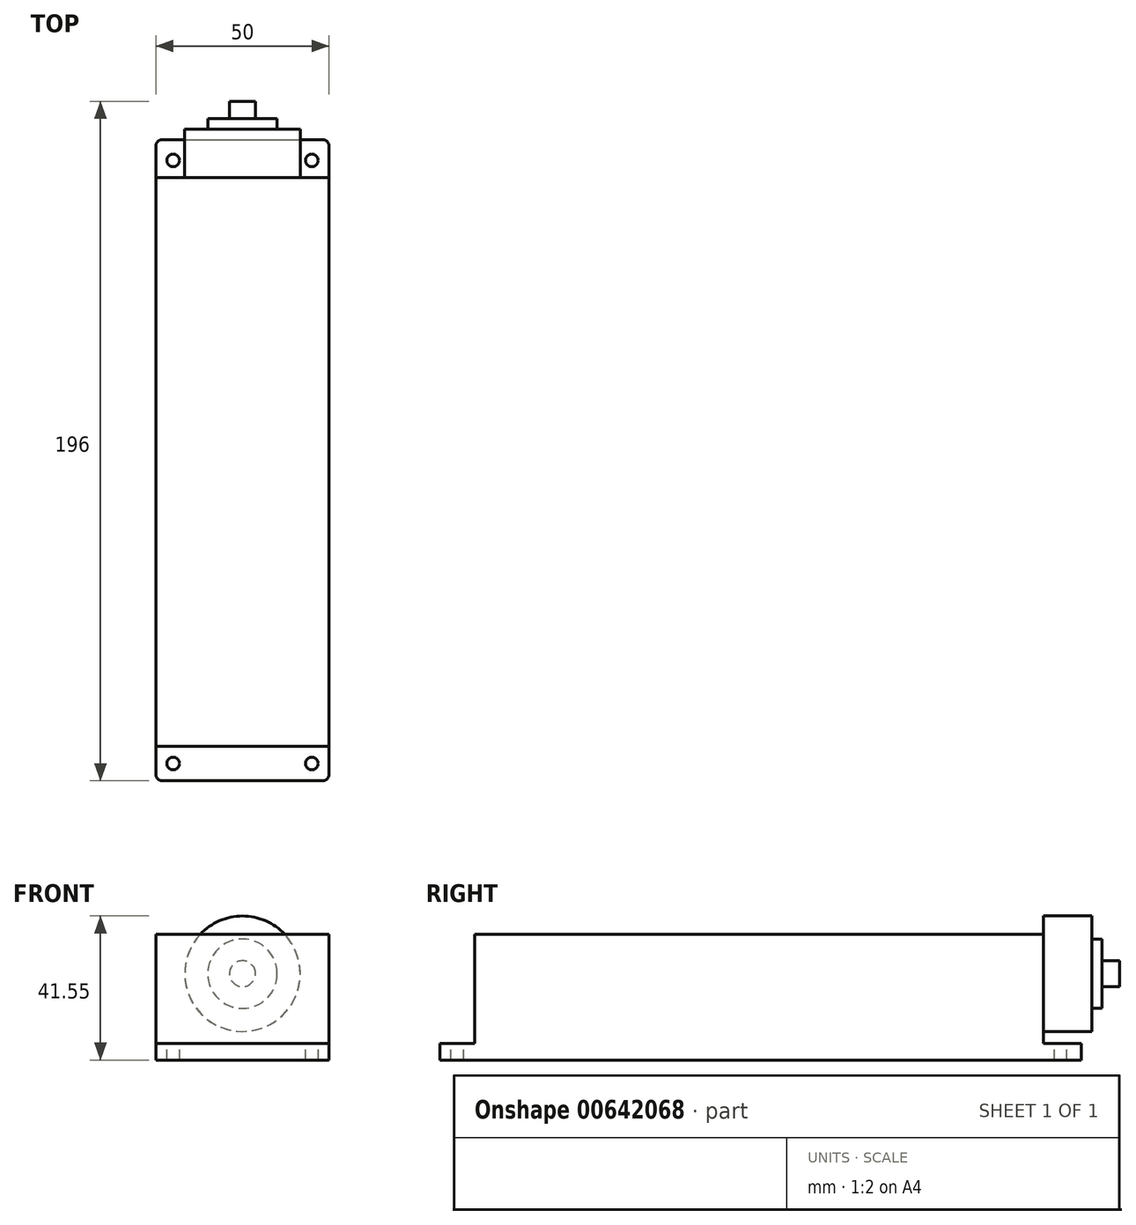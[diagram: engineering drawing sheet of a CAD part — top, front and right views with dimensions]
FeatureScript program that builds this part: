
annotation { "Feature Type Name" : "Feature", "Feature Type Description" : "" }
export const myFeature = defineFeature(function(context is Context, id is Id, definition is map)
    precondition{}
    {
        {
            var Q0;
            Q0=qCreatedBy(makeId("Top.planeOp"),FACE);
            var sketch = newSketch(context, id + "F0", { "sketchPlane" : qUnion([Q0])});
            skLineSegment(sketch, "E0.bottom", {"start": v(2, 0) * mm, "end": v(48, 0) * mm});
            skLineSegment(sketch, "E0.top", {"start": v(2, 185) * mm, "end": v(48, 185) * mm});
            skLineSegment(sketch, "E0.left", {"start": v(0, 2) * mm, "end": v(0, 183) * mm});
            skLineSegment(sketch, "E0.right", {"start": v(50, 2) * mm, "end": v(50, 183) * mm});
            skPoint(sketch, "E1.visualSharp", {"position": v(0, 185) * mm});
            skArc(sketch, "E1.filletArc", {"start": v(2, 185) * mm, "mid": v(0.59, 184.41) * mm, "end": v(0, 183) * mm});
            skPoint(sketch, "E2.visualSharp", {"position": v(50, 185) * mm});
            skArc(sketch, "E2.filletArc", {"start": v(50, 183) * mm, "mid": v(49.41, 184.41) * mm, "end": v(48, 185) * mm});
            skPoint(sketch, "E3.visualSharp", {"position": v(0, 0) * mm});
            skArc(sketch, "E3.filletArc", {"start": v(0, 2) * mm, "mid": v(0.59, 0.59) * mm, "end": v(2, 0) * mm});
            skPoint(sketch, "E4.visualSharp", {"position": v(50, 0) * mm});
            skArc(sketch, "E4.filletArc", {"start": v(48, 0) * mm, "mid": v(49.41, 0.59) * mm, "end": v(50, 2) * mm});
            skSolve(sketch);
        }
        {
            var Q0;
            Q0 = qSketchRegion(id + "F0", true);
            extrude(context, id + "F1", {"entities" : qUnion([Q0]), "depth" : 4.75 * mm, "offsetDistance" : 25 * mm});
        }
        {
            var Q0;
            Q0=makeQuery(id+"F1.opExtrude","CAP_FACE",FACE,{"disambiguationData":[OSD([sQuery(id+"F0.wireOp",EDGE,"E0.bottom"),sQuery(id+"F0.wireOp",EDGE,"E0.top"),sQuery(id+"F0.wireOp",EDGE,"E0.left"),sQuery(id+"F0.wireOp",EDGE,"E0.right")])],"isStart":false});
            var sketch = newSketch(context, id + "F2", { "sketchPlane" : qUnion([Q0])});
            skLineSegment(sketch, "E5.bottom", {"start": v(0, 174) * mm, "end": v(50, 174) * mm});
            skLineSegment(sketch, "E5.top", {"start": v(0, 10) * mm, "end": v(50, 10) * mm});
            skLineSegment(sketch, "E5.left", {"start": v(0, 174) * mm, "end": v(0, 10) * mm});
            skLineSegment(sketch, "E5.right", {"start": v(50, 174) * mm, "end": v(50, 10) * mm});
            skSolve(sketch);
        }
        {
            var Q0;
            Q0 = qSketchRegion(id + "F2", true);
            extrude(context, id + "F3", {"entities" : qUnion([Q0]), "operationType" : NewBodyOperationType.ADD, "depth" : 31.5 * mm, "offsetDistance" : 25 * mm});
        }
        {
            var Q0;
            {var subQ0=sQuery(id+"F0.wireOp",EDGE,"E0.left");var subQ1=sQuery(id+"F0.wireOp",EDGE,"E0.right");var subQ2=sQuery(id+"F0.wireOp",EDGE,"E0.bottom");Q0=makeQuery(id+"F3.boolean.opBoolean","SPLIT",FACE,{"disambiguationData":[TD([makeQuery(id+"F1.opExtrude","SWEPT_FACE",FACE,{"disambiguationData":[OSD([subQ2])]})])],"derivedFrom":makeQuery(id+"F1.opExtrude","CAP_FACE",FACE,{"disambiguationData":[OSD([subQ2,sQuery(id+"F0.wireOp",EDGE,"E0.top"),subQ0,subQ1])],"isStart":false})});}
            var sketch = newSketch(context, id + "F4", { "sketchPlane" : qUnion([Q0])});
            skPoint(sketch, "E6", {"position": v(5, 5) * mm});
            skPoint(sketch, "E7", {"position": v(45, 5) * mm});
            skPoint(sketch, "E8", {"position": v(5, 179) * mm});
            skPoint(sketch, "E9", {"position": v(45, 179) * mm});
            skLineSegment(sketch, "E10", {"start": v(25, 0) * mm, "end": v(25, 184.97) * mm, "construction": true});
            skPoint(sketch, "E10.endSnap0", {"position": v(25, 10) * mm});
            skLineSegment(sketch, "E11", {"start": v(0, 92) * mm, "end": v(50, 92) * mm, "construction": true});
            skSolve(sketch);
        }
        {
            var Q0;
            Q0=sQuery(id+"F4.wireOp",VERTEX,"E8");
            var Q1;
            Q1=sQuery(id+"F4.wireOp",VERTEX,"E9");
            var Q2;
            Q2=sQuery(id+"F4.wireOp",VERTEX,"E6");
            var Q3;
            Q3=sQuery(id+"F4.wireOp",VERTEX,"E7");
            var Q4;
            Q4=makeQuery(id+"F1.opExtrude","SWEPT_BODY",BODY,{"disambiguationData":[OSD([sQuery(id+"F0.wireOp",EDGE,"E0.bottom"),sQuery(id+"F0.wireOp",EDGE,"E0.top"),sQuery(id+"F0.wireOp",EDGE,"E0.left"),sQuery(id+"F0.wireOp",EDGE,"E0.right")])]});
            hole(context, id + "F5", {"style" : HoleStyle.SIMPLE, "endStyle" : HoleEndStyle.THROUGH, "standardTappedOrClearance" : lookupTablePath({ "standard" : "ANSI", "fit" : "Close", "size" : "#6", "type" : "Clearance" }), "standardBlindInLast" : lookupTablePath({ "fit" : "Close", "standard" : "ANSI", "size" : "#6", "type" : "Clearance" }), "holeDiameter" : 3.66 * mm, "majorDiameter" : 5 * mm, "isTappedThrough" : true, "tappedDepth" : 12 * mm, "tapClearance" : 3, "startFromSketch" : true, "locations" : qUnion([Q0, Q1, Q2, Q3]), "scope" : qUnion([Q4])});
        }
        {
            var Q0;
            Q0=makeQuery(id+"F3.opExtrude","SWEPT_FACE",FACE,{"disambiguationData":[OSD([sQuery(id+"F2.wireOp",EDGE,"E5.bottom")])]});
            var sketch = newSketch(context, id + "F6", { "sketchPlane" : qUnion([Q0])});
            skCircle(sketch, "E12", {"center": v(-25, 24.9) * mm, "radius": 16.65 * mm});
            skLineSegment(sketch, "E13", {"start": v(-25, 36.25) * mm, "end": v(-25, 4.75) * mm, "construction": true});
            skSolve(sketch);
        }
        {
            var Q0;
            Q0 = qSketchRegion(id + "F6", true);
            extrude(context, id + "F7", {"entities" : qUnion([Q0]), "operationType" : NewBodyOperationType.ADD, "depth" : 14 * mm, "offsetDistance" : 25 * mm});
        }
        {
            var Q0;
            Q0=makeQuery(id+"F7.opExtrude","CAP_FACE",FACE,{"disambiguationData":[OSD([sQuery(id+"F6.wireOp",EDGE,"E12")])],"isStart":false});
            var sketch = newSketch(context, id + "F8", { "sketchPlane" : qUnion([Q0])});
            skCircle(sketch, "E14", {"center": v(-25, 24.9) * mm, "radius": 10 * mm});
            skSolve(sketch);
        }
        {
            var Q0;
            Q0 = qSketchRegion(id + "F8", true);
            extrude(context, id + "F9", {"entities" : qUnion([Q0]), "operationType" : NewBodyOperationType.ADD, "depth" : 3 * mm, "offsetDistance" : 25 * mm});
        }
        {
            var Q0;
            Q0=makeQuery(id+"F9.opExtrude","CAP_FACE",FACE,{"disambiguationData":[OSD([sQuery(id+"F8.wireOp",EDGE,"E14")])],"isStart":false});
            var sketch = newSketch(context, id + "F10", { "sketchPlane" : qUnion([Q0])});
            skCircle(sketch, "E15", {"center": v(-25, 24.9) * mm, "radius": 3.75 * mm});
            skSolve(sketch);
        }
        {
            var Q0;
            Q0 = qSketchRegion(id + "F10", true);
            extrude(context, id + "F11", {"entities" : qUnion([Q0]), "operationType" : NewBodyOperationType.ADD, "depth" : 5 * mm, "offsetDistance" : 25 * mm});
        }
    });
